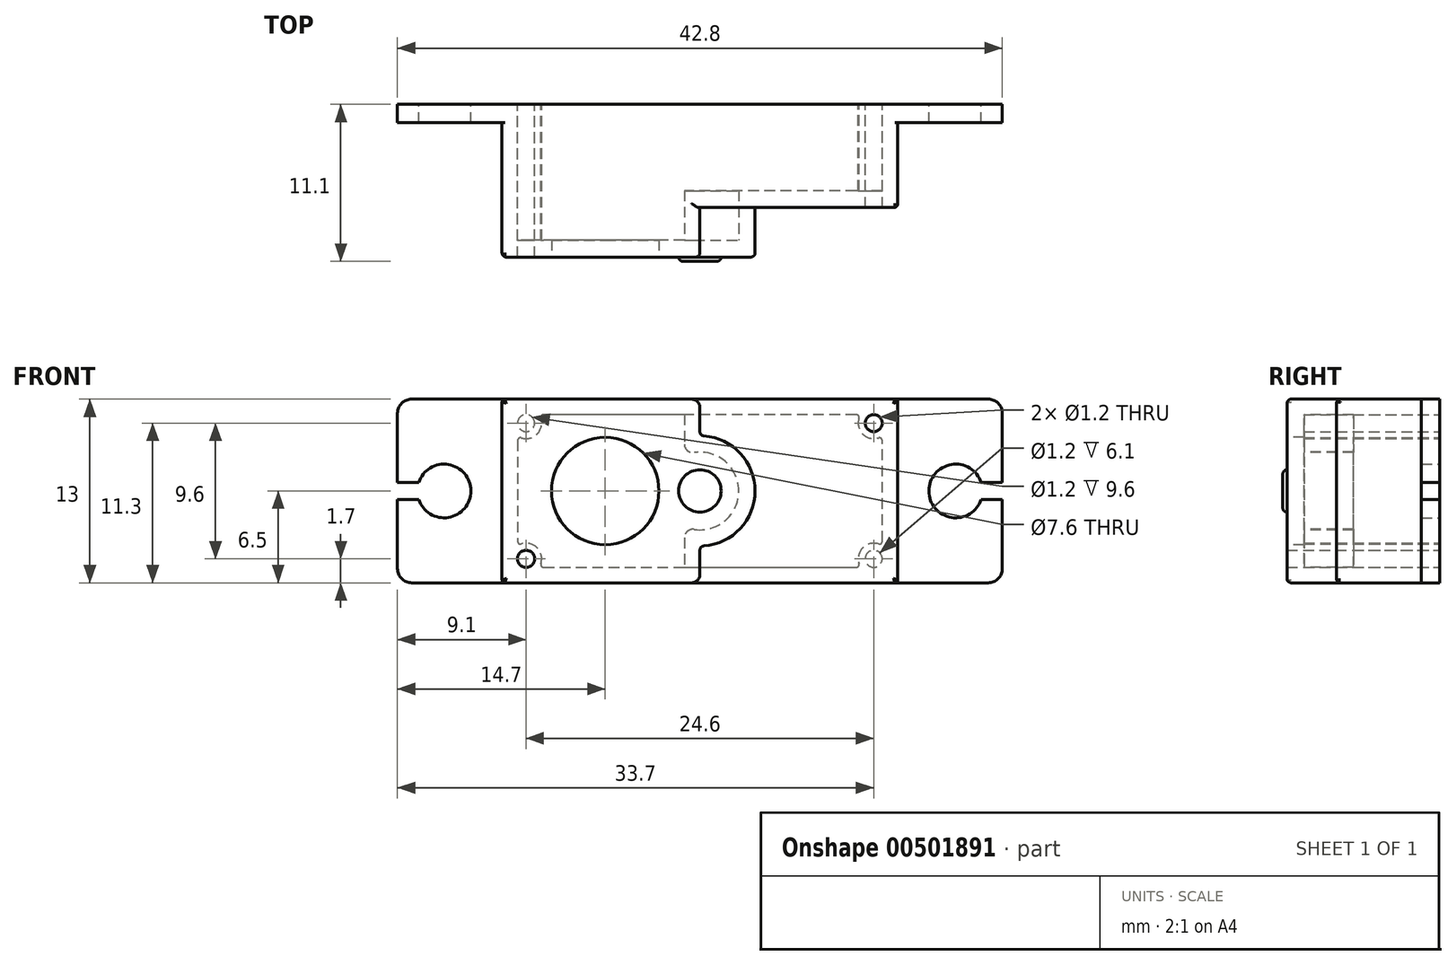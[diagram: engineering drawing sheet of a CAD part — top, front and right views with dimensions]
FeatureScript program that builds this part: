
annotation { "Feature Type Name" : "Feature", "Feature Type Description" : "" }
export const myFeature = defineFeature(function(context is Context, id is Id, definition is map)
    precondition{}
    {
        {
            var Q0;
            Q0=qCreatedBy(makeId("Front.planeOp"),FACE);
            var sketch = newSketch(context, id + "F0", { "sketchPlane" : qUnion([Q0])});
            skLineSegment(sketch, "E0.bottom", {"start": v(0, 0) * mm, "end": v(-14, 0) * mm, "construction": true});
            skLineSegment(sketch, "E0.top", {"start": v(0, 6.5) * mm, "end": v(-13.8, 6.5) * mm});
            skLineSegment(sketch, "E0.left", {"start": v(0, 0) * mm, "end": v(0, 6.5) * mm, "construction": true});
            skLineSegment(sketch, "E0.right", {"start": v(-14, 0) * mm, "end": v(-14, 6.3) * mm});
            skLineSegment(sketch, "E1.0", {"start": v(0, 5.4) * mm, "end": v(-11.06, 5.4) * mm});
            skLineSegment(sketch, "E2.0", {"start": v(-12.9, 0) * mm, "end": v(-12.9, 3.56) * mm});
            skCircle(sketch, "E3", {"center": v(-12.3, 4.8) * mm, "radius": 0.6 * mm});
            skPoint(sketch, "E3.first.point", {"position": v(-12.3, 5.4) * mm});
            skPoint(sketch, "E3.second.point", {"position": v(-12.9, 4.8) * mm});
            skPoint(sketch, "E3.third.point", {"position": v(-12.04, 4.26) * mm});
            skArc(sketch, "E4", {"start": v(-12.64, 3.75) * mm, "mid": v(-11.52, 4.02) * mm, "end": v(-11.25, 5.14) * mm});
            skPoint(sketch, "E5.visualSharp", {"position": v(-11.38, 5.4) * mm});
            skArc(sketch, "E5.filletArc", {"start": v(-11.06, 5.4) * mm, "mid": v(-11.22, 5.32) * mm, "end": v(-11.25, 5.14) * mm});
            skPoint(sketch, "E6.visualSharp", {"position": v(-12.9, 3.88) * mm});
            skArc(sketch, "E6.filletArc", {"start": v(-12.64, 3.75) * mm, "mid": v(-12.82, 3.72) * mm, "end": v(-12.9, 3.56) * mm});
            skArc(sketch, "E7", {"start": v(-12.9, 3.32) * mm, "mid": v(-11.17, 3.67) * mm, "end": v(-10.82, 5.4) * mm});
            skPoint(sketch, "E8.visualSharp", {"position": v(-14, 6.5) * mm});
            skArc(sketch, "E8.filletArc", {"start": v(-13.8, 6.5) * mm, "mid": v(-13.94, 6.44) * mm, "end": v(-14, 6.3) * mm});
            skLineSegment(sketch, "E9.MirrorCS", {"start": v(0, 13) * mm, "end": v(0, 6.5) * mm, "construction": true});
            skLineSegment(sketch, "E10.MirrorCS", {"start": v(0, 5.4) * mm, "end": v(11.06, 5.4) * mm});
            skLineSegment(sketch, "E11.MirrorCS", {"start": v(0, 6.5) * mm, "end": v(13.8, 6.5) * mm});
            skArc(sketch, "E12.MirrorCS", {"start": v(13.8, 6.5) * mm, "mid": v(13.94, 6.44) * mm, "end": v(14, 6.3) * mm});
            skLineSegment(sketch, "E13.MirrorCS", {"start": v(14, 0) * mm, "end": v(14, 6.3) * mm});
            skCircle(sketch, "E14.MirrorC", {"center": v(12.3, 4.8) * mm, "radius": 0.6 * mm});
            skArc(sketch, "E15.MirrorCS", {"start": v(12.64, 3.75) * mm, "mid": v(11.52, 4.02) * mm, "end": v(11.25, 5.14) * mm});
            skArc(sketch, "E16.MirrorCS", {"start": v(11.06, 5.4) * mm, "mid": v(11.22, 5.32) * mm, "end": v(11.25, 5.14) * mm});
            skArc(sketch, "E17.MirrorCS", {"start": v(12.64, 3.75) * mm, "mid": v(12.82, 3.72) * mm, "end": v(12.9, 3.56) * mm});
            skArc(sketch, "E18.MirrorCS", {"start": v(12.9, 3.32) * mm, "mid": v(11.17, 3.67) * mm, "end": v(10.82, 5.4) * mm});
            skLineSegment(sketch, "E19.MirrorCS", {"start": v(12.9, 0) * mm, "end": v(12.9, 3.56) * mm});
            skLineSegment(sketch, "E20.MirrorCS", {"start": v(0, 0) * mm, "end": v(14, 0) * mm, "construction": true});
            skLineSegment(sketch, "E21.MirrorCS", {"start": v(0, -6.5) * mm, "end": v(-13.8, -6.5) * mm});
            skLineSegment(sketch, "E22.MirrorCS", {"start": v(0, -5.4) * mm, "end": v(-11.06, -5.4) * mm});
            skLineSegment(sketch, "E23.MirrorCS", {"start": v(-12.9, 0) * mm, "end": v(-12.9, -3.56) * mm});
            skLineSegment(sketch, "E24.MirrorCS", {"start": v(-14, 0) * mm, "end": v(-14, -6.3) * mm});
            skArc(sketch, "E25.MirrorCS", {"start": v(-12.9, -3.32) * mm, "mid": v(-11.17, -3.67) * mm, "end": v(-10.82, -5.4) * mm});
            skArc(sketch, "E26.MirrorCS", {"start": v(-12.64, -3.75) * mm, "mid": v(-11.52, -4.02) * mm, "end": v(-11.25, -5.14) * mm});
            skCircle(sketch, "E27.MirrorC", {"center": v(-12.3, -4.8) * mm, "radius": 0.6 * mm});
            skArc(sketch, "E28.MirrorCS", {"start": v(-12.64, -3.75) * mm, "mid": v(-12.82, -3.72) * mm, "end": v(-12.9, -3.56) * mm});
            skArc(sketch, "E29.MirrorCS", {"start": v(-11.06, -5.4) * mm, "mid": v(-11.22, -5.32) * mm, "end": v(-11.25, -5.14) * mm});
            skArc(sketch, "E30.MirrorCS", {"start": v(-13.8, -6.5) * mm, "mid": v(-13.94, -6.44) * mm, "end": v(-14, -6.3) * mm});
            skLineSegment(sketch, "E31.MirrorCS", {"start": v(0, -6.5) * mm, "end": v(13.8, -6.5) * mm});
            skLineSegment(sketch, "E32.MirrorCS", {"start": v(0, -5.4) * mm, "end": v(11.06, -5.4) * mm});
            skLineSegment(sketch, "E33.MirrorCS", {"start": v(14, 0) * mm, "end": v(14, -6.3) * mm});
            skLineSegment(sketch, "E34.MirrorCS", {"start": v(12.9, 0) * mm, "end": v(12.9, -3.56) * mm});
            skCircle(sketch, "E35.MirrorC", {"center": v(12.3, -4.8) * mm, "radius": 0.6 * mm});
            skArc(sketch, "E36.MirrorCS", {"start": v(13.8, -6.5) * mm, "mid": v(13.94, -6.44) * mm, "end": v(14, -6.3) * mm});
            skArc(sketch, "E37.MirrorCS", {"start": v(11.06, -5.4) * mm, "mid": v(11.22, -5.32) * mm, "end": v(11.25, -5.14) * mm});
            skArc(sketch, "E38.MirrorCS", {"start": v(12.9, -3.32) * mm, "mid": v(11.17, -3.67) * mm, "end": v(10.82, -5.4) * mm});
            skArc(sketch, "E39.MirrorCS", {"start": v(12.64, -3.75) * mm, "mid": v(11.52, -4.02) * mm, "end": v(11.25, -5.14) * mm});
            skArc(sketch, "E40.MirrorCS", {"start": v(12.64, -3.75) * mm, "mid": v(12.82, -3.72) * mm, "end": v(12.9, -3.56) * mm});
            skSolve(sketch);
        }
        {
            var Q0;
            {var subQ15=sQuery(id+"F0.wireOp",EDGE,"E7");Q0=makeQuery(id+"F0.imprint","IMPRINT",FACE,{"disambiguationData":[TD([[makeQuery(id+"F0.imprint","IMPRINT",EDGE,{"derivedFrom":subQ15}),-1.0]])]});}
            var sketch = newSketch(context, id + "F1", { "sketchPlane" : qUnion([Q0])});
            skLineSegment(sketch, "E41.0", {"start": v(0, 6.5) * mm, "end": v(-13.8, 6.5) * mm});
            skLineSegment(sketch, "E42.0", {"start": v(0, 5.4) * mm, "end": v(-11.06, 5.4) * mm});
            skLineSegment(sketch, "E43.0", {"start": v(-14, 0) * mm, "end": v(-14, 6.3) * mm});
            skCircle(sketch, "E44.0", {"center": v(-12.3, 4.8) * mm, "radius": 0.6 * mm});
            skArc(sketch, "E45.0", {"start": v(-12.64, 3.75) * mm, "mid": v(-11.52, 4.02) * mm, "end": v(-11.25, 5.14) * mm});
            skLineSegment(sketch, "E46.0", {"start": v(0, 6.5) * mm, "end": v(13.8, 6.5) * mm});
            skLineSegment(sketch, "E47.0", {"start": v(0, 5.4) * mm, "end": v(11.06, 5.4) * mm});
            skLineSegment(sketch, "E48.0", {"start": v(0, -5.4) * mm, "end": v(11.06, -5.4) * mm});
            skLineSegment(sketch, "E49.0", {"start": v(0, -6.5) * mm, "end": v(13.8, -6.5) * mm});
            skLineSegment(sketch, "E50.0", {"start": v(0, -5.4) * mm, "end": v(-11.06, -5.4) * mm});
            skLineSegment(sketch, "E51.0", {"start": v(0, -6.5) * mm, "end": v(-13.8, -6.5) * mm});
            skLineSegment(sketch, "E52.0", {"start": v(14, 0) * mm, "end": v(14, 6.3) * mm});
            skLineSegment(sketch, "E53.0", {"start": v(12.9, 0) * mm, "end": v(12.9, 3.56) * mm});
            skLineSegment(sketch, "E54.0", {"start": v(12.9, 0) * mm, "end": v(12.9, -3.56) * mm});
            skLineSegment(sketch, "E55.0", {"start": v(14, 0) * mm, "end": v(14, -6.3) * mm});
            skCircle(sketch, "E56.0", {"center": v(12.3, 4.8) * mm, "radius": 0.6 * mm});
            skCircle(sketch, "E57.0", {"center": v(12.3, -4.8) * mm, "radius": 0.6 * mm});
            skLineSegment(sketch, "E58.0", {"start": v(-12.9, 0) * mm, "end": v(-12.9, 3.56) * mm});
            skLineSegment(sketch, "E59.0", {"start": v(-12.9, 0) * mm, "end": v(-12.9, -3.56) * mm});
            skCircle(sketch, "E60.0", {"center": v(-12.3, -4.8) * mm, "radius": 0.6 * mm});
            skLineSegment(sketch, "E61.0", {"start": v(-14, 0) * mm, "end": v(-14, -6.3) * mm});
            skArc(sketch, "E62.0", {"start": v(-13.8, 6.5) * mm, "mid": v(-13.94, 6.44) * mm, "end": v(-14, 6.3) * mm});
            skArc(sketch, "E63.0", {"start": v(-11.06, 5.4) * mm, "mid": v(-11.22, 5.32) * mm, "end": v(-11.25, 5.14) * mm});
            skArc(sketch, "E64.0", {"start": v(-12.64, 3.75) * mm, "mid": v(-12.82, 3.72) * mm, "end": v(-12.9, 3.56) * mm});
            skArc(sketch, "E65.0", {"start": v(11.06, 5.4) * mm, "mid": v(11.22, 5.32) * mm, "end": v(11.25, 5.14) * mm});
            skArc(sketch, "E66.0", {"start": v(12.64, 3.75) * mm, "mid": v(11.52, 4.02) * mm, "end": v(11.25, 5.14) * mm});
            skArc(sketch, "E67.0", {"start": v(12.64, 3.75) * mm, "mid": v(12.82, 3.72) * mm, "end": v(12.9, 3.56) * mm});
            skArc(sketch, "E68.0", {"start": v(13.8, 6.5) * mm, "mid": v(13.94, 6.44) * mm, "end": v(14, 6.3) * mm});
            skArc(sketch, "E69.0", {"start": v(12.64, -3.75) * mm, "mid": v(11.52, -4.02) * mm, "end": v(11.25, -5.14) * mm});
            skArc(sketch, "E70.0", {"start": v(12.64, -3.75) * mm, "mid": v(12.82, -3.72) * mm, "end": v(12.9, -3.56) * mm});
            skArc(sketch, "E71.0", {"start": v(11.06, -5.4) * mm, "mid": v(11.22, -5.32) * mm, "end": v(11.25, -5.14) * mm});
            skArc(sketch, "E72.0", {"start": v(13.8, -6.5) * mm, "mid": v(13.94, -6.44) * mm, "end": v(14, -6.3) * mm});
            skArc(sketch, "E73.0", {"start": v(-12.64, -3.75) * mm, "mid": v(-11.52, -4.02) * mm, "end": v(-11.25, -5.14) * mm});
            skArc(sketch, "E74.0", {"start": v(-12.64, -3.75) * mm, "mid": v(-12.82, -3.72) * mm, "end": v(-12.9, -3.56) * mm});
            skArc(sketch, "E75.0", {"start": v(-11.06, -5.4) * mm, "mid": v(-11.22, -5.32) * mm, "end": v(-11.25, -5.14) * mm});
            skArc(sketch, "E76.0", {"start": v(-13.8, -6.5) * mm, "mid": v(-13.94, -6.44) * mm, "end": v(-14, -6.3) * mm});
            skSolve(sketch);
        }
        {
            var Q0;
            Q0=makeQuery(id+"F1.imprint","IMPRINT",FACE,{"disambiguationData":[TD([[makeQuery(id+"F1.imprint","IMPRINT",EDGE,{"derivedFrom":sQuery(id+"F1.wireOp",EDGE,"E41.0")}),1.0]])]});
            var sketch = newSketch(context, id + "F2", { "sketchPlane" : qUnion([Q0])});
            skLineSegment(sketch, "E77.0", {"start": v(0, 6.5) * mm, "end": v(13.8, 6.5) * mm});
            skCircle(sketch, "E78.0", {"center": v(12.3, 4.8) * mm, "radius": 0.6 * mm});
            skArc(sketch, "E79.0", {"start": v(12.64, 3.75) * mm, "mid": v(11.52, 4.02) * mm, "end": v(11.25, 5.14) * mm});
            skPoint(sketch, "E80.0", {"position": v(11.22, 5.32) * mm});
            skLineSegment(sketch, "E81.0", {"start": v(0, 5.4) * mm, "end": v(11.06, 5.4) * mm});
            skArc(sketch, "E82.0", {"start": v(12.64, 3.75) * mm, "mid": v(12.82, 3.72) * mm, "end": v(12.9, 3.56) * mm});
            skArc(sketch, "E83.0", {"start": v(11.06, 5.4) * mm, "mid": v(11.22, 5.32) * mm, "end": v(11.25, 5.14) * mm});
            skLineSegment(sketch, "E84.0", {"start": v(0, 6.5) * mm, "end": v(-13.8, 6.5) * mm});
            skLineSegment(sketch, "E85.0", {"start": v(0, 5.4) * mm, "end": v(-11.06, 5.4) * mm});
            skPoint(sketch, "E86.0", {"position": v(-11.52, 4.02) * mm});
            skArc(sketch, "E87.0", {"start": v(-12.64, 3.75) * mm, "mid": v(-11.52, 4.02) * mm, "end": v(-11.25, 5.14) * mm});
            skLineSegment(sketch, "E88.0", {"start": v(-12.9, 0) * mm, "end": v(-12.9, 3.56) * mm});
            skPoint(sketch, "E89.0", {"position": v(-12.9, -1.78) * mm});
            skLineSegment(sketch, "E90.0", {"start": v(-12.9, 0) * mm, "end": v(-12.9, -3.56) * mm});
            skPoint(sketch, "E91.0", {"position": v(-11.52, -4.02) * mm});
            skLineSegment(sketch, "E92.0", {"start": v(0, -5.4) * mm, "end": v(-11.06, -5.4) * mm});
            skLineSegment(sketch, "E93.0", {"start": v(0, -6.5) * mm, "end": v(-13.8, -6.5) * mm});
            skLineSegment(sketch, "E94.0", {"start": v(0, -6.5) * mm, "end": v(13.8, -6.5) * mm});
            skLineSegment(sketch, "E95.0", {"start": v(0, -5.4) * mm, "end": v(11.06, -5.4) * mm});
            skCircle(sketch, "E96.0", {"center": v(-12.3, 4.8) * mm, "radius": 0.6 * mm});
            skPoint(sketch, "E97.0", {"position": v(-12.3, -4.8) * mm});
            skCircle(sketch, "E98.0", {"center": v(-12.3, -4.8) * mm, "radius": 0.6 * mm});
            skArc(sketch, "E99.0", {"start": v(-12.64, -3.75) * mm, "mid": v(-11.52, -4.02) * mm, "end": v(-11.25, -5.14) * mm});
            skPoint(sketch, "E100.0", {"position": v(-11.22, 5.32) * mm});
            skArc(sketch, "E101.0", {"start": v(-12.64, 3.75) * mm, "mid": v(-12.82, 3.72) * mm, "end": v(-12.9, 3.56) * mm});
            skArc(sketch, "E102.0", {"start": v(-11.06, 5.4) * mm, "mid": v(-11.22, 5.32) * mm, "end": v(-11.25, 5.14) * mm});
            skArc(sketch, "E103.0", {"start": v(-12.64, -3.75) * mm, "mid": v(-12.82, -3.72) * mm, "end": v(-12.9, -3.56) * mm});
            skArc(sketch, "E104.0", {"start": v(-11.06, -5.4) * mm, "mid": v(-11.22, -5.32) * mm, "end": v(-11.25, -5.14) * mm});
            skCircle(sketch, "E105.0", {"center": v(12.3, -4.8) * mm, "radius": 0.6 * mm});
            skArc(sketch, "E106.0", {"start": v(12.64, -3.75) * mm, "mid": v(11.52, -4.02) * mm, "end": v(11.25, -5.14) * mm});
            skPoint(sketch, "E107.0", {"position": v(12.82, -3.72) * mm});
            skArc(sketch, "E108.0", {"start": v(11.06, -5.4) * mm, "mid": v(11.22, -5.32) * mm, "end": v(11.25, -5.14) * mm});
            skArc(sketch, "E109.0", {"start": v(12.64, -3.75) * mm, "mid": v(12.82, -3.72) * mm, "end": v(12.9, -3.56) * mm});
            skLineSegment(sketch, "E110.0", {"start": v(12.9, 0) * mm, "end": v(12.9, -3.56) * mm});
            skLineSegment(sketch, "E111.0", {"start": v(12.9, 0) * mm, "end": v(12.9, 3.56) * mm});
            skLineSegment(sketch, "E112.0", {"start": v(21.4, 0.57) * mm, "end": v(21.4, 5.5) * mm});
            skLineSegment(sketch, "E113.0", {"start": v(-21.4, 0.6) * mm, "end": v(-21.4, 5.5) * mm});
            skLineSegment(sketch, "E114", {"start": v(-21.4, -0.6) * mm, "end": v(-21.4, -5.5) * mm});
            skLineSegment(sketch, "E115", {"start": v(-10.46, 6.5) * mm, "end": v(-20.4, 6.5) * mm});
            skLineSegment(sketch, "E116", {"start": v(-9.6, -6.5) * mm, "end": v(-20.4, -6.5) * mm});
            skLineSegment(sketch, "E117", {"start": v(10.93, 6.5) * mm, "end": v(20.4, 6.5) * mm});
            skLineSegment(sketch, "E118", {"start": v(10.93, -6.5) * mm, "end": v(20.4, -6.5) * mm});
            skArc(sketch, "E119.filletArc", {"start": v(21.4, 5.5) * mm, "mid": v(21.1, 6.2) * mm, "end": v(20.4, 6.5) * mm});
            skArc(sketch, "E120.filletArc", {"start": v(20.4, -6.5) * mm, "mid": v(21.1, -6.2) * mm, "end": v(21.4, -5.5) * mm});
            skArc(sketch, "E121.filletArc", {"start": v(-20.4, 6.5) * mm, "mid": v(-21.1, 6.2) * mm, "end": v(-21.4, 5.5) * mm});
            skArc(sketch, "E122.filletArc", {"start": v(-21.4, -5.5) * mm, "mid": v(-21.1, -6.2) * mm, "end": v(-20.4, -6.5) * mm});
            skPoint(sketch, "E123", {"position": v(-21.4, 0) * mm});
            skPoint(sketch, "E124", {"position": v(18.1, 0) * mm});
            skPoint(sketch, "E125", {"position": v(-18.1, 0) * mm});
            skArc(sketch, "E126", {"start": v(-19.9, -0.6) * mm, "mid": v(-16.2, 0) * mm, "end": v(-19.9, 0.6) * mm});
            skArc(sketch, "E127", {"start": v(19.9, 0.6) * mm, "mid": v(16.2, 0) * mm, "end": v(19.9, -0.6) * mm});
            skLineSegment(sketch, "E128", {"start": v(-21.4, 0.6) * mm, "end": v(-19.9, 0.6) * mm});
            skLineSegment(sketch, "E129", {"start": v(21.4, 0.6) * mm, "end": v(19.9, 0.6) * mm});
            skLineSegment(sketch, "E130.MirrorCS", {"start": v(-21.4, -0.6) * mm, "end": v(-19.9, -0.6) * mm});
            skLineSegment(sketch, "E131.MirrorCS", {"start": v(21.4, -0.6) * mm, "end": v(19.9, -0.6) * mm});
            skLineSegment(sketch, "E132.trimOffspring", {"start": v(21.4, -0.6) * mm, "end": v(21.4, -5.5) * mm});
            skSolve(sketch);
        }
        {
            var Q0;
            {var subQ0=sQuery(id+"F2.wireOp",EDGE,"E119.filletArc");Q0=makeQuery(id+"F2.imprint","IMPRINT",FACE,{"disambiguationData":[TD([[makeQuery(id+"F2.imprint","IMPRINT",EDGE,{"derivedFrom":subQ0}),1.0]])]});}
            var Q1;
            {var subQ5=sQuery(id+"F2.wireOp",EDGE,"E77.0");Q1=makeQuery(id+"F2.imprint","IMPRINT",FACE,{"disambiguationData":[TD([[makeQuery(id+"F2.imprint","IMPRINT",EDGE,{"derivedFrom":subQ5}),-1.0]])]});}
            var Q2;
            Q2=makeQuery(id+"F2.imprint","IMPRINT",FACE,{"disambiguationData":[TD([[makeQuery(id+"F2.imprint","IMPRINT",EDGE,{"derivedFrom":sQuery(id+"F2.wireOp",EDGE,"E113.0")}),-1.0]])]});
            extrude(context, id + "F3", {"entities" : qUnion([Q0, Q1, Q2]), "depth" : 1.3 * mm, "offsetDistance" : 25 * mm});
        }
        {
            var Q0;
            Q0=makeQuery(id+"F3.opExtrude","CAP_FACE",FACE,{"disambiguationData":[OSD([sQuery(id+"F2.wireOp",EDGE,"E77.0"),sQuery(id+"F2.wireOp",EDGE,"E78.0"),sQuery(id+"F2.wireOp",EDGE,"E79.0"),sQuery(id+"F2.wireOp",EDGE,"E81.0"),sQuery(id+"F2.wireOp",EDGE,"E82.0"),sQuery(id+"F2.wireOp",EDGE,"E83.0"),sQuery(id+"F2.wireOp",EDGE,"E84.0"),sQuery(id+"F2.wireOp",EDGE,"E85.0"),sQuery(id+"F2.wireOp",EDGE,"E87.0"),sQuery(id+"F2.wireOp",EDGE,"E88.0"),sQuery(id+"F2.wireOp",EDGE,"E90.0"),sQuery(id+"F2.wireOp",EDGE,"E92.0"),sQuery(id+"F2.wireOp",EDGE,"E93.0"),sQuery(id+"F2.wireOp",EDGE,"E94.0"),sQuery(id+"F2.wireOp",EDGE,"E95.0"),sQuery(id+"F2.wireOp",EDGE,"E96.0"),sQuery(id+"F2.wireOp",EDGE,"E98.0"),sQuery(id+"F2.wireOp",EDGE,"E99.0"),sQuery(id+"F2.wireOp",EDGE,"E101.0"),sQuery(id+"F2.wireOp",EDGE,"E102.0"),sQuery(id+"F2.wireOp",EDGE,"E103.0"),sQuery(id+"F2.wireOp",EDGE,"E104.0"),sQuery(id+"F2.wireOp",EDGE,"E105.0"),sQuery(id+"F2.wireOp",EDGE,"E106.0"),sQuery(id+"F2.wireOp",EDGE,"E108.0"),sQuery(id+"F2.wireOp",EDGE,"E109.0"),sQuery(id+"F2.wireOp",EDGE,"E110.0"),sQuery(id+"F2.wireOp",EDGE,"E111.0"),sQuery(id+"F2.wireOp",EDGE,"E112.0"),sQuery(id+"F2.wireOp",EDGE,"E113.0"),sQuery(id+"F2.wireOp",EDGE,"E114"),sQuery(id+"F2.wireOp",EDGE,"E115"),sQuery(id+"F2.wireOp",EDGE,"E116"),sQuery(id+"F2.wireOp",EDGE,"E117"),sQuery(id+"F2.wireOp",EDGE,"E118"),sQuery(id+"F2.wireOp",EDGE,"E119.filletArc"),sQuery(id+"F2.wireOp",EDGE,"E120.filletArc"),sQuery(id+"F2.wireOp",EDGE,"E121.filletArc"),sQuery(id+"F2.wireOp",EDGE,"E122.filletArc"),sQuery(id+"F2.wireOp",EDGE,"E126"),sQuery(id+"F2.wireOp",EDGE,"E127"),sQuery(id+"F2.wireOp",EDGE,"E128"),sQuery(id+"F2.wireOp",EDGE,"E129"),sQuery(id+"F2.wireOp",EDGE,"E130.MirrorCS"),sQuery(id+"F2.wireOp",EDGE,"E131.MirrorCS"),sQuery(id+"F2.wireOp",EDGE,"E132.trimOffspring")])],"isStart":false});
            var sketch = newSketch(context, id + "F4", { "sketchPlane" : qUnion([Q0])});
            skLineSegment(sketch, "E133.0", {"start": v(-14, 0) * mm, "end": v(-14, 6.3) * mm});
            skPoint(sketch, "E134.0", {"position": v(-14, -3.15) * mm});
            skLineSegment(sketch, "E135.0", {"start": v(-14, 0) * mm, "end": v(-14, -6.3) * mm});
            skPoint(sketch, "E136.0", {"position": v(-13.94, 6.44) * mm});
            skArc(sketch, "E137.0", {"start": v(-13.8, 6.5) * mm, "mid": v(-13.94, 6.44) * mm, "end": v(-14, 6.3) * mm});
            skArc(sketch, "E138.0", {"start": v(-13.8, -6.5) * mm, "mid": v(-13.94, -6.44) * mm, "end": v(-14, -6.3) * mm});
            skArc(sketch, "E139.0", {"start": v(13.8, 6.5) * mm, "mid": v(13.94, 6.44) * mm, "end": v(14, 6.3) * mm});
            skLineSegment(sketch, "E140.0", {"start": v(14, 0) * mm, "end": v(14, 6.3) * mm});
            skLineSegment(sketch, "E141.0", {"start": v(14, 0) * mm, "end": v(14, -6.3) * mm});
            skArc(sketch, "E142.0", {"start": v(13.8, -6.5) * mm, "mid": v(13.94, -6.44) * mm, "end": v(14, -6.3) * mm});
            skLineSegment(sketch, "E143", {"start": v(14, 6.3) * mm, "end": v(14, -6.3) * mm});
            skLineSegment(sketch, "E144", {"start": v(-14, 6.3) * mm, "end": v(-14, -6.3) * mm});
            skSolve(sketch);
        }
        {
            var Q0;
            {var subQ3=sQuery(id+"F4.wireOp",EDGE,"E137.0");Q0=makeQuery(id+"F4.imprint","IMPRINT",FACE,{"disambiguationData":[TD([[makeQuery(id+"F4.imprint","IMPRINT",EDGE,{"derivedFrom":subQ3}),1.0]])]});}
            extrude(context, id + "F5", {"entities" : qUnion([Q0]), "operationType" : NewBodyOperationType.ADD, "depth" : 6 * mm, "offsetDistance" : 25 * mm});
        }
        {
            var Q0;
            Q0=makeQuery(id+"F5.opExtrude","CAP_FACE",FACE,{"disambiguationData":[OSD([sQuery(id+"F2.wireOp",EDGE,"E77.0"),sQuery(id+"F2.wireOp",EDGE,"E78.0"),sQuery(id+"F2.wireOp",EDGE,"E79.0"),sQuery(id+"F2.wireOp",EDGE,"E81.0"),sQuery(id+"F2.wireOp",EDGE,"E82.0"),sQuery(id+"F2.wireOp",EDGE,"E83.0"),sQuery(id+"F2.wireOp",EDGE,"E84.0"),sQuery(id+"F2.wireOp",EDGE,"E85.0"),sQuery(id+"F2.wireOp",EDGE,"E87.0"),sQuery(id+"F2.wireOp",EDGE,"E88.0"),sQuery(id+"F2.wireOp",EDGE,"E90.0"),sQuery(id+"F2.wireOp",EDGE,"E92.0"),sQuery(id+"F2.wireOp",EDGE,"E93.0"),sQuery(id+"F2.wireOp",EDGE,"E94.0"),sQuery(id+"F2.wireOp",EDGE,"E95.0"),sQuery(id+"F2.wireOp",EDGE,"E96.0"),sQuery(id+"F2.wireOp",EDGE,"E98.0"),sQuery(id+"F2.wireOp",EDGE,"E99.0"),sQuery(id+"F2.wireOp",EDGE,"E101.0"),sQuery(id+"F2.wireOp",EDGE,"E102.0"),sQuery(id+"F2.wireOp",EDGE,"E103.0"),sQuery(id+"F2.wireOp",EDGE,"E104.0"),sQuery(id+"F2.wireOp",EDGE,"E105.0"),sQuery(id+"F2.wireOp",EDGE,"E106.0"),sQuery(id+"F2.wireOp",EDGE,"E108.0"),sQuery(id+"F2.wireOp",EDGE,"E109.0"),sQuery(id+"F2.wireOp",EDGE,"E110.0"),sQuery(id+"F2.wireOp",EDGE,"E111.0"),sQuery(id+"F2.wireOp",EDGE,"E115"),sQuery(id+"F2.wireOp",EDGE,"E116"),sQuery(id+"F2.wireOp",EDGE,"E117"),sQuery(id+"F2.wireOp",EDGE,"E118"),sQuery(id+"F4.wireOp",EDGE,"E137.0"),sQuery(id+"F4.wireOp",EDGE,"E138.0"),sQuery(id+"F4.wireOp",EDGE,"E139.0"),sQuery(id+"F4.wireOp",EDGE,"E142.0"),sQuery(id+"F4.wireOp",EDGE,"E143"),sQuery(id+"F4.wireOp",EDGE,"E144")])],"isStart":false});
            var sketch = newSketch(context, id + "F6", { "sketchPlane" : qUnion([Q0])});
            skLineSegment(sketch, "E145", {"start": v(0, 5.9) * mm, "end": v(0, 4.19) * mm});
            skLineSegment(sketch, "E146", {"start": v(-1.1, 5.4) * mm, "end": v(-3.12, 3.38) * mm});
            skLineSegment(sketch, "E147", {"start": v(-1.1, 5.4) * mm, "end": v(-1.1, 3.31) * mm});
            skArc(sketch, "E148", {"start": v(0.28, -3.9) * mm, "mid": v(3.9, 0) * mm, "end": v(0.28, 3.9) * mm});
            skArc(sketch, "E149", {"start": v(-0.41, -2.72) * mm, "mid": v(2.75, 0) * mm, "end": v(-0.41, 2.72) * mm});
            skLineSegment(sketch, "E150.trimOffspring", {"start": v(-1.1, -3.31) * mm, "end": v(-1.1, -5.4) * mm});
            skLineSegment(sketch, "E151.trimOffspring", {"start": v(0, -4.19) * mm, "end": v(0, -5.9) * mm});
            skPoint(sketch, "E152.visualSharp", {"position": v(0, 3.9) * mm});
            skArc(sketch, "E152.filletArc", {"start": v(0, 4.19) * mm, "mid": v(0.08, 3.98) * mm, "end": v(0.28, 3.9) * mm});
            skArc(sketch, "E153.filletArc", {"start": v(0.28, -3.9) * mm, "mid": v(0.08, -3.98) * mm, "end": v(0, -4.19) * mm});
            skPoint(sketch, "E154.visualSharp", {"position": v(-1.1, 2.52) * mm});
            skArc(sketch, "E154.filletArc", {"start": v(-1.1, 3.31) * mm, "mid": v(-0.9, 2.86) * mm, "end": v(-0.41, 2.72) * mm});
            skPoint(sketch, "E155.visualSharp", {"position": v(-1.1, -2.52) * mm});
            skArc(sketch, "E155.filletArc", {"start": v(-0.41, -2.72) * mm, "mid": v(-0.9, -2.86) * mm, "end": v(-1.1, -3.31) * mm});
            skLineSegment(sketch, "E156.0", {"start": v(-0.6, 6.5) * mm, "end": v(-13.8, 6.5) * mm});
            skLineSegment(sketch, "E157.0", {"start": v(-0.6, -6.5) * mm, "end": v(-13.8, -6.5) * mm});
            skPoint(sketch, "E158.visualSharp", {"position": v(0, 6.5) * mm});
            skArc(sketch, "E158.filletArc", {"start": v(0, 5.9) * mm, "mid": v(-0.18, 6.32) * mm, "end": v(-0.6, 6.5) * mm});
            skPoint(sketch, "E159.visualSharp", {"position": v(0, -6.5) * mm});
            skArc(sketch, "E159.filletArc", {"start": v(-0.6, -6.5) * mm, "mid": v(-0.18, -6.32) * mm, "end": v(0, -5.9) * mm});
            skSolve(sketch);
        }
        {
            var Q0;
            Q0=makeQuery(id+"F6.imprint","IMPRINT",FACE,{"disambiguationData":[TD([[makeQuery(id+"F6.imprint","IMPRINT",EDGE,{"derivedFrom":sQuery(id+"F6.wireOp",EDGE,"E148")}),-1.0]])]});
            extrude(context, id + "F7", {"entities" : qUnion([Q0]), "operationType" : NewBodyOperationType.ADD, "oppositeDirection" : true, "depth" : 1.2 * mm, "offsetDistance" : 25 * mm});
        }
        {
            var Q0;
            {var subQ9=sQuery(id+"F6.wireOp",EDGE,"E147");Q0=makeQuery(id+"F6.imprint","IMPRINT",FACE,{"disambiguationData":[TD([[makeQuery(id+"F6.imprint","IMPRINT",EDGE,{"derivedFrom":subQ9}),1.0]])]});}
            extrude(context, id + "F8", {"entities" : qUnion([Q0]), "operationType" : NewBodyOperationType.ADD, "oppositeDirection" : true, "depth" : 1.2 * mm, "offsetDistance" : 25 * mm});
        }
        {
            var Q0;
            {var subQ9=sQuery(id+"F6.wireOp",EDGE,"E147");Q0=makeQuery(id+"F6.imprint","IMPRINT",FACE,{"disambiguationData":[TD([[makeQuery(id+"F6.imprint","IMPRINT",EDGE,{"derivedFrom":subQ9}),1.0]])]});}
            extrude(context, id + "F9", {"entities" : qUnion([Q0]), "operationType" : NewBodyOperationType.ADD, "depth" : 3.5 * mm, "offsetDistance" : 25 * mm});
        }
        {
            var Q0;
            Q0=makeQuery(id+"F6.imprint","IMPRINT",FACE,{"disambiguationData":[TD([[makeQuery(id+"F6.imprint","IMPRINT",EDGE,{"derivedFrom":sQuery(id+"F6.wireOp",EDGE,"E156.0")}),-1.0]])]});
            extrude(context, id + "F10", {"entities" : qUnion([Q0]), "operationType" : NewBodyOperationType.ADD, "depth" : 3.5 * mm, "offsetDistance" : 25 * mm});
        }
        {
            var Q0;
            {var subQ0=sQuery(id+"F6.wireOp",EDGE,"E151.trimOffspring");var subQ1=sQuery(id+"F6.wireOp",EDGE,"E145");var subQ2=sQuery(id+"F2.wireOp",EDGE,"E95.0");var subQ3=sQuery(id+"F2.wireOp",EDGE,"E92.0");var subQ4=sQuery(id+"F2.wireOp",EDGE,"E85.0");var subQ5=sQuery(id+"F2.wireOp",EDGE,"E81.0");Q0=makeQuery(id+"F10.boolean.opBoolean","MERGE",FACE,{"derivedFrom":[makeQuery(id+"F9.opExtrude","CAP_FACE",FACE,{"disambiguationData":[OSD([subQ5,subQ4,subQ3,subQ2,subQ1,sQuery(id+"F6.wireOp",EDGE,"E147"),sQuery(id+"F6.wireOp",EDGE,"E148"),sQuery(id+"F6.wireOp",EDGE,"E149"),sQuery(id+"F6.wireOp",EDGE,"E150.trimOffspring"),subQ0,sQuery(id+"F6.wireOp",EDGE,"E152.filletArc"),sQuery(id+"F6.wireOp",EDGE,"E153.filletArc"),sQuery(id+"F6.wireOp",EDGE,"E154.filletArc"),sQuery(id+"F6.wireOp",EDGE,"E155.filletArc")])],"isStart":false}),makeQuery(id+"F10.opExtrude","CAP_FACE",FACE,{"disambiguationData":[OSD([subQ5,subQ4,sQuery(id+"F2.wireOp",EDGE,"E87.0"),sQuery(id+"F2.wireOp",EDGE,"E88.0"),sQuery(id+"F2.wireOp",EDGE,"E90.0"),subQ3,subQ2,sQuery(id+"F2.wireOp",EDGE,"E96.0"),sQuery(id+"F2.wireOp",EDGE,"E98.0"),sQuery(id+"F2.wireOp",EDGE,"E99.0"),sQuery(id+"F2.wireOp",EDGE,"E101.0"),sQuery(id+"F2.wireOp",EDGE,"E102.0"),sQuery(id+"F2.wireOp",EDGE,"E103.0"),sQuery(id+"F2.wireOp",EDGE,"E104.0"),sQuery(id+"F4.wireOp",EDGE,"E137.0"),sQuery(id+"F4.wireOp",EDGE,"E138.0"),sQuery(id+"F4.wireOp",EDGE,"E144"),subQ1,subQ0,sQuery(id+"F6.wireOp",EDGE,"E156.0"),sQuery(id+"F6.wireOp",EDGE,"E157.0"),sQuery(id+"F6.wireOp",EDGE,"E158.filletArc"),sQuery(id+"F6.wireOp",EDGE,"E159.filletArc")])],"isStart":false})]});}
            var sketch = newSketch(context, id + "F11", { "sketchPlane" : qUnion([Q0])});
            skSolve(sketch);
        }
        {
            var Q0;
            Q0=makeQuery(id+"F11.imprint","IMPRINT",FACE,{"disambiguationData":[TD([[makeQuery(id+"F11.imprint","IMPRINT",EDGE,{"derivedFrom":makeQuery(id+"F9.opExtrude","CAP_EDGE",EDGE,{"disambiguationData":[OSD([sQuery(id+"F6.wireOp",EDGE,"E147")])],"isStart":false})}),-1.0]])]});
            extrude(context, id + "F12", {"entities" : qUnion([Q0]), "operationType" : NewBodyOperationType.ADD, "oppositeDirection" : true, "depth" : 1.2 * mm, "offsetDistance" : 25 * mm});
        }
        {
            var Q0;
            {var subQ0=sQuery(id+"F6.wireOp",EDGE,"E155.filletArc");var subQ1=sQuery(id+"F6.wireOp",EDGE,"E154.filletArc");var subQ2=sQuery(id+"F6.wireOp",EDGE,"E150.trimOffspring");var subQ3=sQuery(id+"F6.wireOp",EDGE,"E149");var subQ4=sQuery(id+"F6.wireOp",EDGE,"E147");var subQ5=sQuery(id+"F2.wireOp",EDGE,"E104.0");var subQ6=sQuery(id+"F2.wireOp",EDGE,"E103.0");var subQ7=sQuery(id+"F2.wireOp",EDGE,"E102.0");var subQ8=sQuery(id+"F2.wireOp",EDGE,"E101.0");var subQ9=sQuery(id+"F2.wireOp",EDGE,"E99.0");var subQ10=sQuery(id+"F2.wireOp",EDGE,"E95.0");var subQ11=sQuery(id+"F2.wireOp",EDGE,"E92.0");var subQ12=sQuery(id+"F2.wireOp",EDGE,"E90.0");var subQ13=sQuery(id+"F2.wireOp",EDGE,"E88.0");var subQ14=sQuery(id+"F2.wireOp",EDGE,"E87.0");var subQ15=sQuery(id+"F2.wireOp",EDGE,"E85.0");var subQ16=sQuery(id+"F2.wireOp",EDGE,"E81.0");var subQ17=sQuery(id+"F6.wireOp",EDGE,"E151.trimOffspring");var subQ18=sQuery(id+"F6.wireOp",EDGE,"E145");Q0=makeQuery(id+"F12.boolean.opBoolean","MERGE",FACE,{"derivedFrom":[makeQuery(id+"F10.boolean.opBoolean","MERGE",FACE,{"derivedFrom":[makeQuery(id+"F9.opExtrude","CAP_FACE",FACE,{"disambiguationData":[OSD([subQ16,subQ15,subQ11,subQ10,subQ18,subQ4,sQuery(id+"F6.wireOp",EDGE,"E148"),subQ3,subQ2,subQ17,sQuery(id+"F6.wireOp",EDGE,"E152.filletArc"),sQuery(id+"F6.wireOp",EDGE,"E153.filletArc"),subQ1,subQ0])],"isStart":false}),makeQuery(id+"F10.opExtrude","CAP_FACE",FACE,{"disambiguationData":[OSD([subQ16,subQ15,subQ14,subQ13,subQ12,subQ11,subQ10,sQuery(id+"F2.wireOp",EDGE,"E96.0"),sQuery(id+"F2.wireOp",EDGE,"E98.0"),subQ9,subQ8,subQ7,subQ6,subQ5,sQuery(id+"F4.wireOp",EDGE,"E137.0"),sQuery(id+"F4.wireOp",EDGE,"E138.0"),sQuery(id+"F4.wireOp",EDGE,"E144"),subQ18,subQ17,sQuery(id+"F6.wireOp",EDGE,"E156.0"),sQuery(id+"F6.wireOp",EDGE,"E157.0"),sQuery(id+"F6.wireOp",EDGE,"E158.filletArc"),sQuery(id+"F6.wireOp",EDGE,"E159.filletArc")])],"isStart":false})]}),makeQuery(id+"F12.opExtrude","CAP_FACE",FACE,{"disambiguationData":[OSD([subQ16,subQ15,subQ14,subQ13,subQ12,subQ11,subQ10,subQ9,subQ8,subQ7,subQ6,subQ5,subQ4,subQ3,subQ2,subQ1,subQ0])],"isStart":true})]});}
            var sketch = newSketch(context, id + "F13", { "sketchPlane" : qUnion([Q0])});
            skCircle(sketch, "E160", {"center": v(0, 0) * mm, "radius": 1.5 * mm});
            skSolve(sketch);
        }
        {
            var Q0;
            Q0 = qSketchRegion(id + "F13", true);
            extrude(context, id + "F14", {"entities" : qUnion([Q0]), "operationType" : NewBodyOperationType.ADD, "depth" : 0.3 * mm, "offsetDistance" : 25 * mm});
        }
        {
            var Q0;
            {var subQ0=sQuery(id+"F6.wireOp",EDGE,"E155.filletArc");var subQ1=sQuery(id+"F6.wireOp",EDGE,"E154.filletArc");var subQ2=sQuery(id+"F6.wireOp",EDGE,"E150.trimOffspring");var subQ3=sQuery(id+"F6.wireOp",EDGE,"E149");var subQ4=sQuery(id+"F6.wireOp",EDGE,"E147");var subQ5=sQuery(id+"F2.wireOp",EDGE,"E104.0");var subQ6=sQuery(id+"F2.wireOp",EDGE,"E103.0");var subQ7=sQuery(id+"F2.wireOp",EDGE,"E102.0");var subQ8=sQuery(id+"F2.wireOp",EDGE,"E101.0");var subQ9=sQuery(id+"F2.wireOp",EDGE,"E99.0");var subQ10=sQuery(id+"F2.wireOp",EDGE,"E95.0");var subQ11=sQuery(id+"F2.wireOp",EDGE,"E92.0");var subQ12=sQuery(id+"F2.wireOp",EDGE,"E90.0");var subQ13=sQuery(id+"F2.wireOp",EDGE,"E88.0");var subQ14=sQuery(id+"F2.wireOp",EDGE,"E87.0");var subQ15=sQuery(id+"F2.wireOp",EDGE,"E85.0");var subQ16=sQuery(id+"F2.wireOp",EDGE,"E81.0");var subQ17=sQuery(id+"F6.wireOp",EDGE,"E151.trimOffspring");var subQ18=sQuery(id+"F6.wireOp",EDGE,"E145");Q0=makeQuery(id+"F12.boolean.opBoolean","MERGE",FACE,{"derivedFrom":[makeQuery(id+"F10.boolean.opBoolean","MERGE",FACE,{"derivedFrom":[makeQuery(id+"F9.opExtrude","CAP_FACE",FACE,{"disambiguationData":[OSD([subQ16,subQ15,subQ11,subQ10,subQ18,subQ4,sQuery(id+"F6.wireOp",EDGE,"E148"),subQ3,subQ2,subQ17,sQuery(id+"F6.wireOp",EDGE,"E152.filletArc"),sQuery(id+"F6.wireOp",EDGE,"E153.filletArc"),subQ1,subQ0])],"isStart":false}),makeQuery(id+"F10.opExtrude","CAP_FACE",FACE,{"disambiguationData":[OSD([subQ16,subQ15,subQ14,subQ13,subQ12,subQ11,subQ10,sQuery(id+"F2.wireOp",EDGE,"E96.0"),sQuery(id+"F2.wireOp",EDGE,"E98.0"),subQ9,subQ8,subQ7,subQ6,subQ5,sQuery(id+"F4.wireOp",EDGE,"E137.0"),sQuery(id+"F4.wireOp",EDGE,"E138.0"),sQuery(id+"F4.wireOp",EDGE,"E144"),subQ18,subQ17,sQuery(id+"F6.wireOp",EDGE,"E156.0"),sQuery(id+"F6.wireOp",EDGE,"E157.0"),sQuery(id+"F6.wireOp",EDGE,"E158.filletArc"),sQuery(id+"F6.wireOp",EDGE,"E159.filletArc")])],"isStart":false})]}),makeQuery(id+"F12.opExtrude","CAP_FACE",FACE,{"disambiguationData":[OSD([subQ16,subQ15,subQ14,subQ13,subQ12,subQ11,subQ10,subQ9,subQ8,subQ7,subQ6,subQ5,subQ4,subQ3,subQ2,subQ1,subQ0])],"isStart":true})]});}
            var sketch = newSketch(context, id + "F15", { "sketchPlane" : qUnion([Q0])});
            skSolve(sketch);
        }
        {
            var Q0;
            Q0=makeQuery(id+"F15.imprint","IMPRINT",FACE,{"disambiguationData":[TD([[makeQuery(id+"F15.imprint","IMPRINT",EDGE,{"derivedFrom":makeQuery(id+"F10.opExtrude","CAP_EDGE",EDGE,{"disambiguationData":[OSD([sQuery(id+"F2.wireOp",EDGE,"E96.0")])],"isStart":false})}),1.0]])]});
            var Q1;
            Q1=makeQuery(id+"F15.imprint","IMPRINT",FACE,{"disambiguationData":[TD([[makeQuery(id+"F15.imprint","IMPRINT",EDGE,{"derivedFrom":makeQuery(id+"F10.opExtrude","CAP_EDGE",EDGE,{"disambiguationData":[OSD([sQuery(id+"F2.wireOp",EDGE,"E98.0")])],"isStart":false})}),-1.0]])]});
            extrude(context, id + "F16", {"entities" : qUnion([Q0, Q1]), "operationType" : NewBodyOperationType.ADD, "oppositeDirection" : true, "depth" : 1.2 * mm, "offsetDistance" : 25 * mm});
        }
        {
            var Q0;
            Q0=makeQuery(id+"F6.imprint","IMPRINT",FACE,{"disambiguationData":[TD([[makeQuery(id+"F6.imprint","IMPRINT",EDGE,{"derivedFrom":makeQuery(id+"F5.opExtrude","CAP_EDGE",EDGE,{"disambiguationData":[OSD([sQuery(id+"F2.wireOp",EDGE,"E78.0")])],"isStart":false})}),-1.0]])]});
            var Q1;
            Q1=makeQuery(id+"F6.imprint","IMPRINT",FACE,{"disambiguationData":[TD([[makeQuery(id+"F6.imprint","IMPRINT",EDGE,{"derivedFrom":makeQuery(id+"F5.opExtrude","CAP_EDGE",EDGE,{"disambiguationData":[OSD([sQuery(id+"F2.wireOp",EDGE,"E105.0")])],"isStart":false})}),1.0]])]});
            extrude(context, id + "F17", {"entities" : qUnion([Q0, Q1]), "operationType" : NewBodyOperationType.ADD, "oppositeDirection" : true, "depth" : 1.2 * mm, "offsetDistance" : 25 * mm});
        }
        {
            var Q0;
            Q0=makeQuery(id+"F10.opExtrude","CAP_EDGE",EDGE,{"disambiguationData":[OSD([sQuery(id+"F6.wireOp",EDGE,"E157.0")])],"isStart":false});
            fillet(context, id + "F18", {"entities" : qUnion([Q0]), "radius" : 0.3 * mm, "tangentPropagation" : true, "allowEdgeOverflow" : false});
        }
        {
            var Q0;
            Q0=makeQuery(id+"F5.opExtrude","CAP_EDGE",EDGE,{"disambiguationData":[OSD([sQuery(id+"F2.wireOp",EDGE,"E93.0"),sQuery(id+"F2.wireOp",EDGE,"E94.0"),sQuery(id+"F2.wireOp",EDGE,"E116"),sQuery(id+"F2.wireOp",EDGE,"E118")])],"isStart":false});
            var Q1;
            Q1=makeQuery(id+"F14.opExtrude","CAP_EDGE",EDGE,{"disambiguationData":[OSD([sQuery(id+"F13.wireOp",EDGE,"E160")])],"isStart":false});
            fillet(context, id + "F19", {"entities" : qUnion([Q0, Q1]), "radius" : 0.3 * mm, "tangentPropagation" : true, "allowEdgeOverflow" : false});
        }
        {
            var Q0;
            {var subQ0=sQuery(id+"F2.wireOp",EDGE,"E98.0");var subQ1=sQuery(id+"F2.wireOp",EDGE,"E96.0");var subQ2=sQuery(id+"F6.wireOp",EDGE,"E155.filletArc");var subQ3=sQuery(id+"F6.wireOp",EDGE,"E154.filletArc");var subQ4=sQuery(id+"F6.wireOp",EDGE,"E150.trimOffspring");var subQ5=sQuery(id+"F6.wireOp",EDGE,"E149");var subQ6=sQuery(id+"F6.wireOp",EDGE,"E147");var subQ7=sQuery(id+"F2.wireOp",EDGE,"E104.0");var subQ8=sQuery(id+"F2.wireOp",EDGE,"E103.0");var subQ9=sQuery(id+"F2.wireOp",EDGE,"E102.0");var subQ10=sQuery(id+"F2.wireOp",EDGE,"E101.0");var subQ11=sQuery(id+"F2.wireOp",EDGE,"E99.0");var subQ12=sQuery(id+"F2.wireOp",EDGE,"E95.0");var subQ13=sQuery(id+"F2.wireOp",EDGE,"E92.0");var subQ14=sQuery(id+"F2.wireOp",EDGE,"E90.0");var subQ15=sQuery(id+"F2.wireOp",EDGE,"E88.0");var subQ16=sQuery(id+"F2.wireOp",EDGE,"E87.0");var subQ17=sQuery(id+"F2.wireOp",EDGE,"E85.0");var subQ18=sQuery(id+"F2.wireOp",EDGE,"E81.0");var subQ19=sQuery(id+"F6.wireOp",EDGE,"E151.trimOffspring");var subQ20=sQuery(id+"F6.wireOp",EDGE,"E145");Q0=makeQuery(id+"F16.boolean.opBoolean","MERGE",FACE,{"derivedFrom":[makeQuery(id+"F12.boolean.opBoolean","MERGE",FACE,{"derivedFrom":[makeQuery(id+"F10.boolean.opBoolean","MERGE",FACE,{"derivedFrom":[makeQuery(id+"F9.opExtrude","CAP_FACE",FACE,{"disambiguationData":[OSD([subQ18,subQ17,subQ13,subQ12,subQ20,subQ6,sQuery(id+"F6.wireOp",EDGE,"E148"),subQ5,subQ4,subQ19,sQuery(id+"F6.wireOp",EDGE,"E152.filletArc"),sQuery(id+"F6.wireOp",EDGE,"E153.filletArc"),subQ3,subQ2])],"isStart":false}),makeQuery(id+"F10.opExtrude","CAP_FACE",FACE,{"disambiguationData":[OSD([subQ18,subQ17,subQ16,subQ15,subQ14,subQ13,subQ12,subQ1,subQ0,subQ11,subQ10,subQ9,subQ8,subQ7,sQuery(id+"F4.wireOp",EDGE,"E137.0"),sQuery(id+"F4.wireOp",EDGE,"E138.0"),sQuery(id+"F4.wireOp",EDGE,"E144"),subQ20,subQ19,sQuery(id+"F6.wireOp",EDGE,"E156.0"),sQuery(id+"F6.wireOp",EDGE,"E157.0"),sQuery(id+"F6.wireOp",EDGE,"E158.filletArc"),sQuery(id+"F6.wireOp",EDGE,"E159.filletArc")])],"isStart":false})]}),makeQuery(id+"F12.opExtrude","CAP_FACE",FACE,{"disambiguationData":[OSD([subQ18,subQ17,subQ16,subQ15,subQ14,subQ13,subQ12,subQ11,subQ10,subQ9,subQ8,subQ7,subQ6,subQ5,subQ4,subQ3,subQ2])],"isStart":true})]}),makeQuery(id+"F16.opExtrude","CAP_FACE",FACE,{"disambiguationData":[OSD([subQ1])],"isStart":true}),makeQuery(id+"F16.opExtrude","CAP_FACE",FACE,{"disambiguationData":[OSD([subQ0])],"isStart":true})]});}
            var sketch = newSketch(context, id + "F20", { "sketchPlane" : qUnion([Q0])});
            skCircle(sketch, "E161", {"center": v(-6.7, 0) * mm, "radius": 3.8 * mm});
            skPoint(sketch, "E161.centerSnap0", {"position": v(-13.7, 0) * mm});
            skSolve(sketch);
        }
        {
            var Q0;
            Q0=makeQuery(id+"F20.imprint","IMPRINT",FACE,{"disambiguationData":[TD([[makeQuery(id+"F20.imprint","IMPRINT",EDGE,{"derivedFrom":sQuery(id+"F20.wireOp",EDGE,"E161")}),1.0]])]});
            extrude(context, id + "F21", {"entities" : qUnion([Q0]), "operationType" : NewBodyOperationType.REMOVE, "oppositeDirection" : true, "depth" : 1.2 * mm, "offsetDistance" : 25 * mm});
        }
    });
